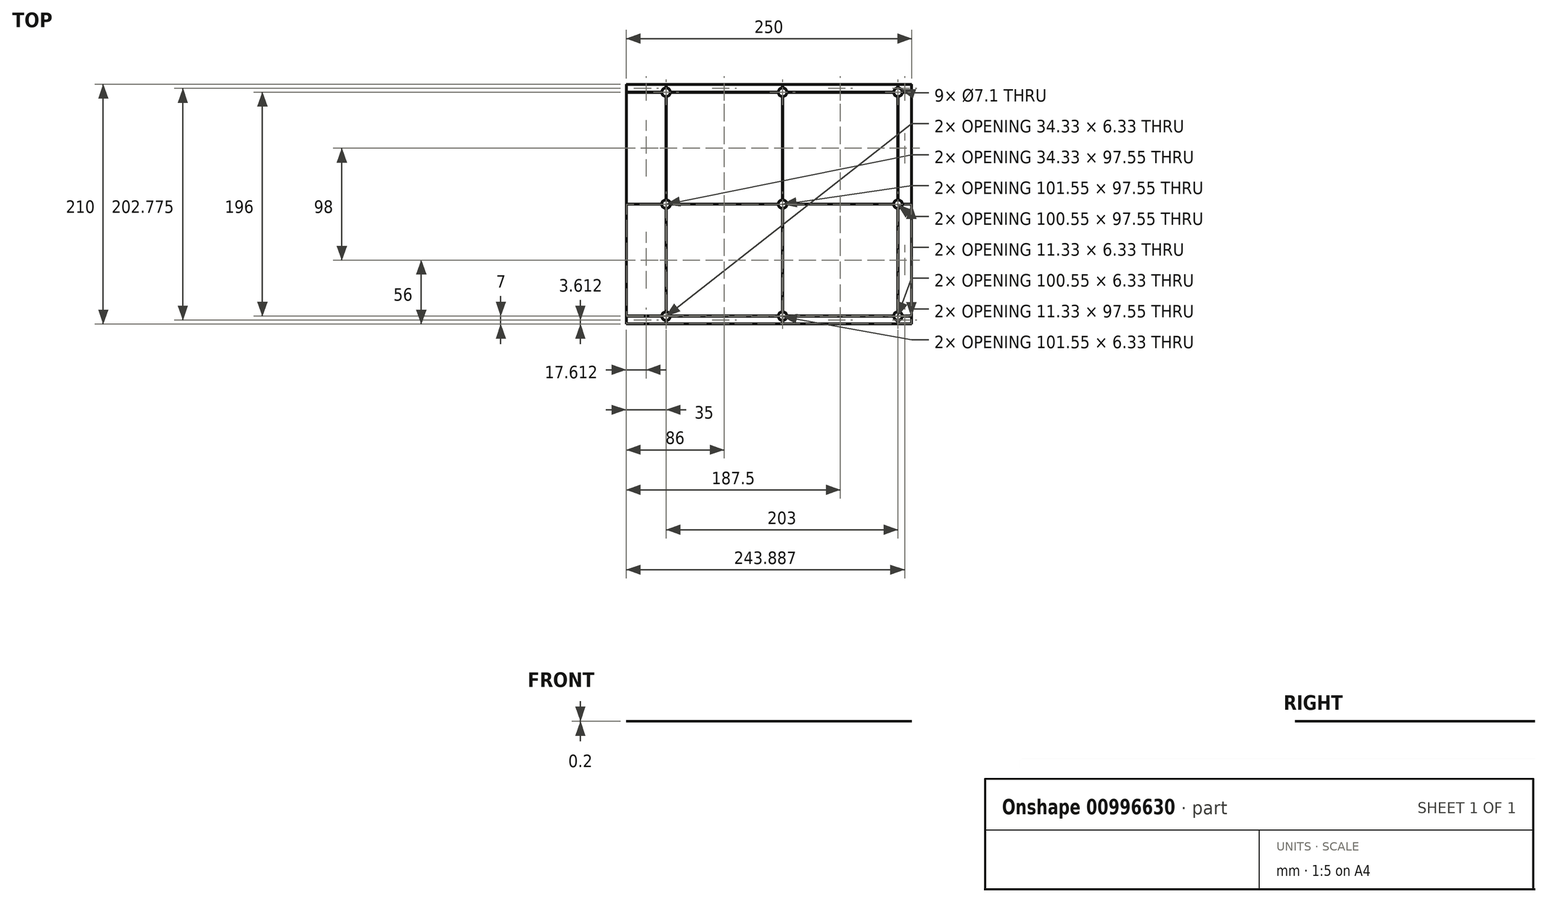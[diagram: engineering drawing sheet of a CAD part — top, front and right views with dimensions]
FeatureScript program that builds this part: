
annotation { "Feature Type Name" : "Feature", "Feature Type Description" : "" }
export const myFeature = defineFeature(function(context is Context, id is Id, definition is map)
    precondition{}
    {
        {
            var Q0;
            Q0=qCreatedBy(makeId("Top.planeOp"),FACE);
            var sketch = newSketch(context, id + "F0", { "sketchPlane" : qUnion([Q0])});
            skLineSegment(sketch, "E0.bottom", {"start": v(125, -105) * mm, "end": v(-125, -105) * mm});
            skLineSegment(sketch, "E0.top", {"start": v(125, 105) * mm, "end": v(-125, 105) * mm});
            skLineSegment(sketch, "E0.left", {"start": v(125, -105) * mm, "end": v(125, 105) * mm});
            skLineSegment(sketch, "E0.right", {"start": v(-125, -105) * mm, "end": v(-125, 105) * mm});
            skPoint(sketch, "E0.middle", {"position": v(0, 0) * mm});
            skLineSegment(sketch, "E1.0", {"start": v(124.55, -104.55) * mm, "end": v(113.23, -104.55) * mm});
            skLineSegment(sketch, "E1.1", {"start": v(124.55, -104.55) * mm, "end": v(124.55, -98.22) * mm});
            skLineSegment(sketch, "E1.2", {"start": v(124.55, 104.55) * mm, "end": v(113.22, 104.55) * mm});
            skLineSegment(sketch, "E1.3", {"start": v(-124.55, -104.55) * mm, "end": v(-124.55, -98.23) * mm});
            skArc(sketch, "E2", {"start": v(-90.23, 102) * mm, "mid": v(-92.83, 100.83) * mm, "end": v(-94, 98.22) * mm});
            skCircle(sketch, "E3.0", {"center": v(-90, 98) * mm, "radius": 3.55 * mm});
            skLineSegment(sketch, "E4", {"start": v(-90.23, 102) * mm, "end": v(-90.23, 104.55) * mm});
            skLineSegment(sketch, "E5", {"start": v(-89.78, 104.55) * mm, "end": v(-89.78, 102) * mm});
            skLineSegment(sketch, "E6", {"start": v(-124.55, 98.23) * mm, "end": v(-94, 98.23) * mm});
            skLineSegment(sketch, "E7", {"start": v(-94, 97.78) * mm, "end": v(-124.55, 97.78) * mm});
            skLineSegment(sketch, "E8.trimOffspring", {"start": v(-90.23, 104.55) * mm, "end": v(-124.55, 104.55) * mm});
            skArc(sketch, "E9.trimOffspring", {"start": v(-94, 97.77) * mm, "mid": v(-92.83, 95.17) * mm, "end": v(-90.23, 94) * mm});
            skLineSegment(sketch, "E10.trimOffspring", {"start": v(-124.55, 98.22) * mm, "end": v(-124.55, 104.55) * mm});
            skArc(sketch, "E11", {"start": v(8, 97.78) * mm, "mid": v(9.17, 95.17) * mm, "end": v(11.78, 94) * mm});
            skCircle(sketch, "E12", {"center": v(12, 98) * mm, "radius": 3.55 * mm});
            skLineSegment(sketch, "E13", {"start": v(-86, 97.77) * mm, "end": v(8, 97.78) * mm});
            skLineSegment(sketch, "E14", {"start": v(8, 98.23) * mm, "end": v(-86, 98.23) * mm});
            skArc(sketch, "E15.trimOffspring", {"start": v(-86, 98.22) * mm, "mid": v(-87.17, 100.83) * mm, "end": v(-89.78, 102) * mm});
            skLineSegment(sketch, "E16", {"start": v(11.78, 102) * mm, "end": v(11.78, 104.55) * mm});
            skLineSegment(sketch, "E17", {"start": v(12.23, 104.55) * mm, "end": v(12.23, 102) * mm});
            skLineSegment(sketch, "E18.trimOffspring", {"start": v(11.78, 104.55) * mm, "end": v(-89.78, 104.55) * mm});
            skArc(sketch, "E19.trimOffspring", {"start": v(11.78, 102) * mm, "mid": v(9.17, 100.83) * mm, "end": v(8, 98.23) * mm});
            skArc(sketch, "E20", {"start": v(109, 97.78) * mm, "mid": v(110.17, 95.17) * mm, "end": v(112.77, 94) * mm});
            skCircle(sketch, "E21", {"center": v(113, 98) * mm, "radius": 3.55 * mm});
            skLineSegment(sketch, "E22", {"start": v(16, 98.23) * mm, "end": v(109, 98.23) * mm});
            skLineSegment(sketch, "E23", {"start": v(109, 97.78) * mm, "end": v(16, 97.78) * mm});
            skArc(sketch, "E24.trimOffspring", {"start": v(16, 98.23) * mm, "mid": v(14.83, 100.83) * mm, "end": v(12.23, 102) * mm});
            skLineSegment(sketch, "E25", {"start": v(112.77, 104.55) * mm, "end": v(112.77, 102) * mm});
            skLineSegment(sketch, "E26", {"start": v(113.22, 102) * mm, "end": v(113.22, 104.55) * mm});
            skLineSegment(sketch, "E27.trimOffspring", {"start": v(112.77, 104.55) * mm, "end": v(12.23, 104.55) * mm});
            skArc(sketch, "E28.trimOffspring", {"start": v(112.77, 102) * mm, "mid": v(110.17, 100.83) * mm, "end": v(109, 98.23) * mm});
            skLineSegment(sketch, "E29", {"start": v(117, 98.23) * mm, "end": v(124.55, 98.23) * mm});
            skLineSegment(sketch, "E30", {"start": v(124.55, 97.78) * mm, "end": v(117, 97.78) * mm});
            skLineSegment(sketch, "E31.trimOffspring", {"start": v(124.55, 98.23) * mm, "end": v(124.55, 104.55) * mm});
            skArc(sketch, "E32.trimOffspring", {"start": v(117, 98.23) * mm, "mid": v(115.83, 100.83) * mm, "end": v(113.22, 102) * mm});
            skArc(sketch, "E33", {"start": v(-94, -0.22) * mm, "mid": v(-92.83, -2.83) * mm, "end": v(-90.23, -4) * mm});
            skCircle(sketch, "E34", {"center": v(-90, 0) * mm, "radius": 3.55 * mm});
            skLineSegment(sketch, "E35", {"start": v(-124.55, 0.23) * mm, "end": v(-94, 0.23) * mm});
            skLineSegment(sketch, "E36", {"start": v(-94, -0.22) * mm, "end": v(-124.55, -0.22) * mm});
            skLineSegment(sketch, "E37.trimOffspring", {"start": v(-124.55, 0.23) * mm, "end": v(-124.55, 97.77) * mm});
            skLineSegment(sketch, "E38", {"start": v(-90.23, 4) * mm, "end": v(-90.23, 94) * mm});
            skLineSegment(sketch, "E39", {"start": v(-89.77, 94) * mm, "end": v(-89.77, 4) * mm});
            skArc(sketch, "E40.trimOffspring", {"start": v(-90.23, 4) * mm, "mid": v(-92.83, 2.83) * mm, "end": v(-94, 0.23) * mm});
            skArc(sketch, "E41.trimOffspring", {"start": v(-89.77, 94) * mm, "mid": v(-87.17, 95.17) * mm, "end": v(-86, 97.77) * mm});
            skArc(sketch, "E42", {"start": v(8, -0.22) * mm, "mid": v(9.17, -2.83) * mm, "end": v(11.78, -4) * mm});
            skCircle(sketch, "E43", {"center": v(12, 0) * mm, "radius": 3.55 * mm});
            skLineSegment(sketch, "E44", {"start": v(-86, 0.23) * mm, "end": v(8, 0.23) * mm});
            skLineSegment(sketch, "E45", {"start": v(8, -0.22) * mm, "end": v(-86, -0.22) * mm});
            skArc(sketch, "E46.trimOffspring", {"start": v(-86, 0.23) * mm, "mid": v(-87.17, 2.83) * mm, "end": v(-89.77, 4) * mm});
            skLineSegment(sketch, "E47", {"start": v(11.78, 4) * mm, "end": v(11.78, 94) * mm});
            skLineSegment(sketch, "E48", {"start": v(12.23, 94) * mm, "end": v(12.23, 4) * mm});
            skArc(sketch, "E49.trimOffspring", {"start": v(11.78, 4) * mm, "mid": v(9.17, 2.83) * mm, "end": v(8, 0.23) * mm});
            skArc(sketch, "E50.trimOffspring", {"start": v(12.23, 94) * mm, "mid": v(14.83, 95.17) * mm, "end": v(16, 97.78) * mm});
            skArc(sketch, "E51", {"start": v(109, -0.23) * mm, "mid": v(110.17, -2.83) * mm, "end": v(112.77, -4) * mm});
            skCircle(sketch, "E52", {"center": v(113, 0) * mm, "radius": 3.55 * mm});
            skLineSegment(sketch, "E53", {"start": v(16, 0.23) * mm, "end": v(109, 0.23) * mm});
            skLineSegment(sketch, "E54", {"start": v(109, -0.22) * mm, "end": v(16, -0.22) * mm});
            skArc(sketch, "E55.trimOffspring", {"start": v(16, 0.23) * mm, "mid": v(14.83, 2.83) * mm, "end": v(12.23, 4) * mm});
            skLineSegment(sketch, "E56", {"start": v(112.77, 4) * mm, "end": v(112.77, 94) * mm});
            skLineSegment(sketch, "E57", {"start": v(113.23, 94) * mm, "end": v(113.23, 4) * mm});
            skArc(sketch, "E58.trimOffspring", {"start": v(112.77, 4) * mm, "mid": v(110.17, 2.83) * mm, "end": v(109, 0.23) * mm});
            skArc(sketch, "E59.trimOffspring", {"start": v(113.22, 94) * mm, "mid": v(115.83, 95.17) * mm, "end": v(117, 97.78) * mm});
            skLineSegment(sketch, "E60", {"start": v(117, 0.23) * mm, "end": v(124.55, 0.23) * mm});
            skLineSegment(sketch, "E61", {"start": v(124.55, -0.22) * mm, "end": v(117, -0.22) * mm});
            skArc(sketch, "E62.trimOffspring", {"start": v(117, 0.23) * mm, "mid": v(115.83, 2.83) * mm, "end": v(113.23, 4) * mm});
            skLineSegment(sketch, "E63.trimOffspring", {"start": v(124.55, 0.23) * mm, "end": v(124.55, 97.78) * mm});
            skArc(sketch, "E64", {"start": v(-94, -98.23) * mm, "mid": v(-92.83, -100.83) * mm, "end": v(-90.23, -102) * mm});
            skCircle(sketch, "E65", {"center": v(-90, -98) * mm, "radius": 3.55 * mm});
            skLineSegment(sketch, "E66", {"start": v(-124.55, -97.78) * mm, "end": v(-94, -97.78) * mm});
            skLineSegment(sketch, "E67", {"start": v(-94, -98.23) * mm, "end": v(-124.55, -98.23) * mm});
            skLineSegment(sketch, "E68.trimOffspring", {"start": v(-124.55, -97.78) * mm, "end": v(-124.55, -0.22) * mm});
            skLineSegment(sketch, "E69", {"start": v(-90.23, -94) * mm, "end": v(-90.23, -4) * mm});
            skLineSegment(sketch, "E70", {"start": v(-89.77, -4) * mm, "end": v(-89.77, -94) * mm});
            skArc(sketch, "E71.trimOffspring", {"start": v(-90.23, -94) * mm, "mid": v(-92.83, -95.17) * mm, "end": v(-94, -97.78) * mm});
            skArc(sketch, "E72.trimOffspring", {"start": v(-89.77, -4) * mm, "mid": v(-87.17, -2.83) * mm, "end": v(-86, -0.22) * mm});
            skArc(sketch, "E73", {"start": v(8, -98.22) * mm, "mid": v(9.17, -100.83) * mm, "end": v(11.78, -102) * mm});
            skCircle(sketch, "E74", {"center": v(12, -98) * mm, "radius": 3.55 * mm});
            skLineSegment(sketch, "E75", {"start": v(-86, -97.78) * mm, "end": v(8, -97.78) * mm});
            skLineSegment(sketch, "E76", {"start": v(8, -98.22) * mm, "end": v(-86, -98.22) * mm});
            skArc(sketch, "E77.trimOffspring", {"start": v(-86, -97.78) * mm, "mid": v(-87.17, -95.17) * mm, "end": v(-89.77, -94) * mm});
            skLineSegment(sketch, "E78", {"start": v(-90.23, -102) * mm, "end": v(-90.23, -104.55) * mm});
            skLineSegment(sketch, "E79", {"start": v(-89.78, -102) * mm, "end": v(-89.78, -104.55) * mm});
            skArc(sketch, "E80.trimOffspring", {"start": v(-89.78, -102) * mm, "mid": v(-87.17, -100.83) * mm, "end": v(-86, -98.22) * mm});
            skLineSegment(sketch, "E81.trimOffspring", {"start": v(-90.23, -104.55) * mm, "end": v(-124.55, -104.55) * mm});
            skLineSegment(sketch, "E82", {"start": v(11.78, -4) * mm, "end": v(11.78, -94) * mm});
            skLineSegment(sketch, "E83", {"start": v(12.22, -94) * mm, "end": v(12.22, -4) * mm});
            skArc(sketch, "E84.trimOffspring", {"start": v(12.22, -4) * mm, "mid": v(14.83, -2.83) * mm, "end": v(16, -0.22) * mm});
            skArc(sketch, "E85.trimOffspring", {"start": v(11.78, -94) * mm, "mid": v(9.17, -95.17) * mm, "end": v(8, -97.78) * mm});
            skLineSegment(sketch, "E86", {"start": v(11.78, -102) * mm, "end": v(11.78, -104.55) * mm});
            skLineSegment(sketch, "E87", {"start": v(12.22, -102) * mm, "end": v(12.22, -104.55) * mm});
            skArc(sketch, "E88.trimOffspring", {"start": v(12.22, -102) * mm, "mid": v(14.83, -100.83) * mm, "end": v(16, -98.22) * mm});
            skLineSegment(sketch, "E89.trimOffspring", {"start": v(11.78, -104.55) * mm, "end": v(-89.78, -104.55) * mm});
            skArc(sketch, "E90", {"start": v(109, -98.22) * mm, "mid": v(110.17, -100.83) * mm, "end": v(112.77, -102) * mm});
            skCircle(sketch, "E91", {"center": v(113, -98) * mm, "radius": 3.55 * mm});
            skLineSegment(sketch, "E92", {"start": v(16, -97.78) * mm, "end": v(109, -97.78) * mm});
            skLineSegment(sketch, "E93", {"start": v(109, -98.22) * mm, "end": v(16, -98.22) * mm});
            skArc(sketch, "E94.trimOffspring", {"start": v(16, -97.78) * mm, "mid": v(14.83, -95.17) * mm, "end": v(12.22, -94) * mm});
            skLineSegment(sketch, "E95", {"start": v(117, -97.78) * mm, "end": v(124.55, -97.78) * mm});
            skLineSegment(sketch, "E96", {"start": v(117, -98.22) * mm, "end": v(124.55, -98.22) * mm});
            skArc(sketch, "E97.trimOffspring", {"start": v(117, -97.78) * mm, "mid": v(115.83, -95.17) * mm, "end": v(113.23, -94) * mm});
            skLineSegment(sketch, "E98.trimOffspring", {"start": v(124.55, -97.78) * mm, "end": v(124.55, -0.22) * mm});
            skLineSegment(sketch, "E99", {"start": v(112.77, -4) * mm, "end": v(112.77, -94) * mm});
            skLineSegment(sketch, "E100", {"start": v(113.23, -94) * mm, "end": v(113.23, -4) * mm});
            skArc(sketch, "E101.trimOffspring", {"start": v(113.23, -4) * mm, "mid": v(115.83, -2.83) * mm, "end": v(117, -0.22) * mm});
            skArc(sketch, "E102.trimOffspring", {"start": v(112.77, -94) * mm, "mid": v(110.17, -95.17) * mm, "end": v(109, -97.78) * mm});
            skLineSegment(sketch, "E103", {"start": v(112.77, -102) * mm, "end": v(112.77, -104.55) * mm});
            skLineSegment(sketch, "E104", {"start": v(113.23, -102) * mm, "end": v(113.23, -104.55) * mm});
            skArc(sketch, "E105.trimOffspring", {"start": v(113.23, -102) * mm, "mid": v(115.83, -100.83) * mm, "end": v(117, -98.22) * mm});
            skLineSegment(sketch, "E106.trimOffspring", {"start": v(112.77, -104.55) * mm, "end": v(12.22, -104.55) * mm});
            skSolve(sketch);
        }
        {
            var Q0;
            Q0=makeQuery(id+"F0.imprint","IMPRINT",FACE,{"disambiguationData":[TD([[makeQuery(id+"F0.imprint","IMPRINT",EDGE,{"derivedFrom":sQuery(id+"F0.wireOp",EDGE,"E0.bottom")}),-1.0]])]});
            extrude(context, id + "F1", {"entities" : qUnion([Q0]), "depth" : 0.2 * mm, "offsetDistance" : 25 * mm});
        }
    });
